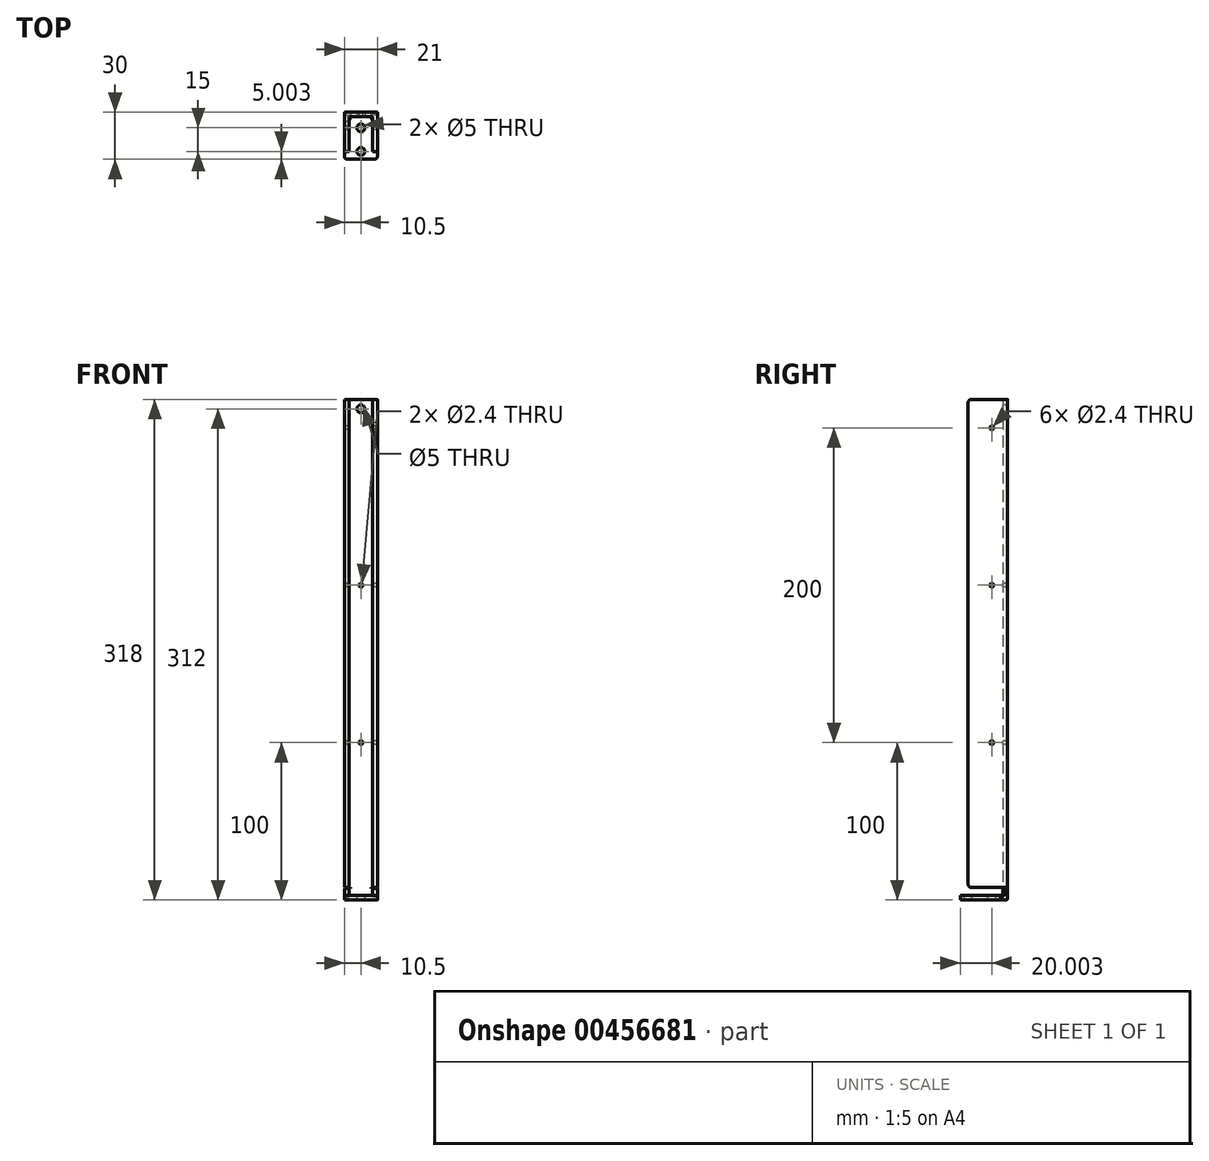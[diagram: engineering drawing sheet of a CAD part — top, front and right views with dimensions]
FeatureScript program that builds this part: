
annotation { "Feature Type Name" : "Feature", "Feature Type Description" : "" }
export const myFeature = defineFeature(function(context is Context, id is Id, definition is map)
    precondition{}
    {
        {
            var Q0;
            Q0=qCreatedBy(makeId("Right.planeOp"),FACE);
            var sketch = newSketch(context, id + "F0", { "sketchPlane" : qUnion([Q0])});
            skLineSegment(sketch, "E0", {"start": v(-7.6, 0) * mm, "end": v(22.4, 0) * mm});
            skLineSegment(sketch, "E1", {"start": v(22.4, 0) * mm, "end": v(22.4, 318) * mm});
            skLineSegment(sketch, "E2", {"start": v(22.4, 318) * mm, "end": v(19.4, 318) * mm});
            skLineSegment(sketch, "E3", {"start": v(19.4, 318) * mm, "end": v(19.4, 3) * mm});
            skLineSegment(sketch, "E4", {"start": v(19.4, 3) * mm, "end": v(-7.6, 3) * mm});
            skLineSegment(sketch, "E5", {"start": v(-7.6, 3) * mm, "end": v(-7.6, 0) * mm});
            skSolve(sketch);
        }
        {
            var Q0;
            Q0=qSketchRegion(id+"F0",true);
            extrude(context, id + "F1", {"entities" : qUnion([Q0]), "depth" : 15 * mm});
        }
        {
            var Q0;
            Q0=makeQuery(id+"F1.opExtrude","SWEPT_FACE",FACE,{"disambiguationData":[OSD([sQuery(id+"F0.wireOp",EDGE,"E1")])]});
            var sketch = newSketch(context, id + "F2", { "sketchPlane" : qUnion([Q0])});
            skLineSegment(sketch, "E6.bottom", {"start": v(0, 8) * mm, "end": v(3, 8) * mm});
            skLineSegment(sketch, "E6.top", {"start": v(0, 318) * mm, "end": v(3, 318) * mm});
            skLineSegment(sketch, "E6.left", {"start": v(0, 8) * mm, "end": v(0, 318) * mm});
            skLineSegment(sketch, "E6.right", {"start": v(3, 8) * mm, "end": v(3, 318) * mm});
            skLineSegment(sketch, "E7.bottom", {"start": v(-15, 318) * mm, "end": v(-18, 318) * mm});
            skLineSegment(sketch, "E7.top", {"start": v(-15, 8) * mm, "end": v(-18, 8) * mm});
            skLineSegment(sketch, "E7.left", {"start": v(-15, 318) * mm, "end": v(-15, 8) * mm});
            skLineSegment(sketch, "E7.right", {"start": v(-18, 318) * mm, "end": v(-18, 8) * mm});
            skSolve(sketch);
        }
        {
            var Q0;
            Q0=qSketchRegion(id+"F2",true);
            extrude(context, id + "F3", {"entities" : qUnion([Q0]), "operationType" : NewBodyOperationType.ADD, "oppositeDirection" : true, "depth" : 25 * mm});
        }
        {
            var Q0;
            Q0=makeQuery(id+"F1.opExtrude","SWEPT_FACE",FACE,{"disambiguationData":[OSD([sQuery(id+"F0.wireOp",EDGE,"E4")])]});
            var sketch = newSketch(context, id + "F4", { "sketchPlane" : qUnion([Q0])});
            skCircle(sketch, "E8", {"center": v(7.5, -2.6) * mm, "radius": 2.5 * mm});
            skCircle(sketch, "E9", {"center": v(7.5, 12.4) * mm, "radius": 2.5 * mm});
            skCircle(sketch, "E10", {"center": v(7.5, 12.4) * mm, "radius": 4.5 * mm, "construction": true});
            skCircle(sketch, "E11", {"center": v(7.5, -2.6) * mm, "radius": 4.46 * mm, "construction": true});
            skSolve(sketch);
        }
        {
            var Q0;
            Q0=qSketchRegion(id+"F4",true);
            extrude(context, id + "F5", {"entities" : qUnion([Q0]), "operationType" : NewBodyOperationType.REMOVE, "oppositeDirection" : true, "depth" : 3 * mm});
        }
        {
            var Q0;
            Q0=makeQuery(id+"F1.opExtrude","SWEPT_FACE",FACE,{"disambiguationData":[OSD([sQuery(id+"F0.wireOp",EDGE,"E3")])]});
            var sketch = newSketch(context, id + "F6", { "sketchPlane" : qUnion([Q0])});
            skLineSegment(sketch, "E12.bottom", {"start": v(0, 8) * mm, "end": v(1, 8) * mm});
            skLineSegment(sketch, "E12.top", {"start": v(0, 7.5) * mm, "end": v(1, 7.5) * mm});
            skLineSegment(sketch, "E12.left", {"start": v(0, 8) * mm, "end": v(0, 7.5) * mm});
            skLineSegment(sketch, "E12.right", {"start": v(1, 8) * mm, "end": v(1, 7.5) * mm});
            skLineSegment(sketch, "E13.bottom", {"start": v(15, 8) * mm, "end": v(14, 8) * mm});
            skLineSegment(sketch, "E13.top", {"start": v(15, 7.5) * mm, "end": v(14, 7.5) * mm});
            skLineSegment(sketch, "E13.left", {"start": v(15, 8) * mm, "end": v(15, 7.5) * mm});
            skLineSegment(sketch, "E13.right", {"start": v(14, 8) * mm, "end": v(14, 7.5) * mm});
            skSolve(sketch);
        }
        {
            var Q0;
            Q0=qSketchRegion(id+"F6",true);
            extrude(context, id + "F7", {"entities" : qUnion([Q0]), "operationType" : NewBodyOperationType.REMOVE, "oppositeDirection" : true, "depth" : 3 * mm});
        }
        {
            var Q0;
            Q0=makeQuery(id+"F1.opExtrude","SWEPT_EDGE",EDGE,{"disambiguationData":[OSD([sQuery(id+"F0.wireOp",EDGE,"E3"),sQuery(id+"F0.wireOp",EDGE,"E4")])]});
            var Q1;
            Q1=makeQuery(id+"F1.opExtrude","SWEPT_EDGE",EDGE,{"disambiguationData":[OSD([sQuery(id+"F0.wireOp",EDGE,"E0"),sQuery(id+"F0.wireOp",EDGE,"E1")])]});
            var Q2;
            {var subQ0=sQuery(id+"F0.wireOp",EDGE,"E3");Q2=makeQuery(id+"F3.boolean.opBoolean","SPLIT",EDGE,{"disambiguationData":[topologyDisambiguationEdgeConnected([makeQuery(id+"F3.opExtrude","SWEPT_FACE",FACE,{"disambiguationData":[OSD([sQuery(id+"F2.wireOp",EDGE,"E6.left")])]})])],"derivedFrom":makeQuery(id+"F1.opExtrude","CAP_EDGE",EDGE,{"disambiguationData":[OSD([subQ0])],"isStart":true})});}
            var Q3;
            Q3=makeQuery(id+"F3.opExtrude","CAP_EDGE",EDGE,{"disambiguationData":[OSD([sQuery(id+"F2.wireOp",EDGE,"E6.right")])],"isStart":true});
            var Q4;
            Q4=makeQuery(id+"F3.opExtrude","CAP_EDGE",EDGE,{"disambiguationData":[OSD([sQuery(id+"F2.wireOp",EDGE,"E7.right")])],"isStart":true});
            var Q5;
            {var subQ0=sQuery(id+"F0.wireOp",EDGE,"E3");Q5=makeQuery(id+"F3.boolean.opBoolean","SPLIT",EDGE,{"disambiguationData":[topologyDisambiguationEdgeConnected([makeQuery(id+"F3.opExtrude","SWEPT_FACE",FACE,{"disambiguationData":[OSD([sQuery(id+"F2.wireOp",EDGE,"E7.left")])]})])],"derivedFrom":makeQuery(id+"F1.opExtrude","CAP_EDGE",EDGE,{"disambiguationData":[OSD([subQ0])],"isStart":false})});}
            var Q6;
            Q6=makeQuery(id+"FqQp6dOOzKqRe4i_1.boolean.opBoolean","COPY",EDGE,{"derivedFrom":makeQuery(id+"FqQp6dOOzKqRe4i_1.opExtrude","CAP_EDGE",EDGE,{"disambiguationData":[OSD([sQuery(id+"FuQxhJIuyBZaYl9_1.wireOp",EDGE,"ZrIXolOl-gWOG-G3Ii-Wei4-7PRN7w7ykNvu.left")])],"isStart":false})});
            var Q7;
            Q7=makeQuery(id+"FqQp6dOOzKqRe4i_1.boolean.opBoolean","COPY",EDGE,{"derivedFrom":makeQuery(id+"FqQp6dOOzKqRe4i_1.opExtrude","CAP_EDGE",EDGE,{"disambiguationData":[OSD([sQuery(id+"FuQxhJIuyBZaYl9_1.wireOp",EDGE,"ZrIXolOl-gWOG-G3Ii-Wei4-7PRN7w7ykNvu.right")])],"isStart":false})});
            fillet(context, id + "F8", {"entities" : qUnion([Q0, Q1, Q2, Q3, Q4, Q5, Q6, Q7]), "radius" : 1 * mm, "tangentPropagation" : true, "allowEdgeOverflow" : false});
        }
        {
            var Q0;
            Q0=makeQuery(id+"F1.opExtrude","SWEPT_FACE",FACE,{"disambiguationData":[OSD([sQuery(id+"F0.wireOp",EDGE,"E3")])]});
            var sketch = newSketch(context, id + "F9", { "sketchPlane" : qUnion([Q0])});
            skCircle(sketch, "E14", {"center": v(7.5, 312) * mm, "radius": 2.5 * mm});
            skPoint(sketch, "E14.centerSnap0", {"position": v(7.5, 318) * mm});
            skCircle(sketch, "E15", {"center": v(7.5, 100) * mm, "radius": 1.2 * mm});
            skPoint(sketch, "E15.centerSnap0", {"position": v(7.5, 4) * mm});
            skCircle(sketch, "E16", {"center": v(7.5, 200) * mm, "radius": 1.2 * mm});
            skSolve(sketch);
        }
        {
            var Q0;
            Q0=qSketchRegion(id+"F9",true);
            extrude(context, id + "F10", {"entities" : qUnion([Q0]), "operationType" : NewBodyOperationType.REMOVE, "oppositeDirection" : true, "depth" : 3 * mm});
        }
        {
            var Q0;
            Q0=makeQuery(id+"F3.opExtrude","SWEPT_FACE",FACE,{"disambiguationData":[OSD([sQuery(id+"F2.wireOp",EDGE,"E6.right")])]});
            var sketch = newSketch(context, id + "F11", { "sketchPlane" : qUnion([Q0])});
            skCircle(sketch, "E17", {"center": v(-12.4, 300) * mm, "radius": 1.2 * mm});
            skCircle(sketch, "E18", {"center": v(-12.4, 100) * mm, "radius": 1.2 * mm});
            skLineSegment(sketch, "E19", {"start": v(-14.4, 98) * mm, "end": v(-14.4, -49.26) * mm, "construction": true});
            skLineSegment(sketch, "E20", {"start": v(103.6, 103.79) * mm, "end": v(103.6, -31.5) * mm, "construction": true});
            skLineSegment(sketch, "E21", {"start": v(-16.4, 98.96) * mm, "end": v(-16.4, 90.53) * mm, "construction": true});
            skLineSegment(sketch, "E22", {"start": v(105.6, 89.13) * mm, "end": v(105.6, 82.47) * mm, "construction": true});
            skCircle(sketch, "E23", {"center": v(-12.4, 200) * mm, "radius": 1.2 * mm});
            skSolve(sketch);
        }
        {
            var Q0;
            Q0=qSketchRegion(id+"F11",true);
            extrude(context, id + "F12", {"entities" : qUnion([Q0]), "operationType" : NewBodyOperationType.REMOVE, "oppositeDirection" : true, "depth" : 34.2 * mm});
        }
        {
            var Q0;
            Q0=makeQuery(id+"F1.opExtrude","CAP_FACE",FACE,{"disambiguationData":[OSD([sQuery(id+"F0.wireOp",EDGE,"E0"),sQuery(id+"F0.wireOp",EDGE,"E1"),sQuery(id+"F0.wireOp",EDGE,"E2"),sQuery(id+"F0.wireOp",EDGE,"E3"),sQuery(id+"F0.wireOp",EDGE,"E4"),sQuery(id+"F0.wireOp",EDGE,"E5")])],"isStart":true});
            extrude(context, id + "F13", {"entities" : qUnion([Q0]), "operationType" : NewBodyOperationType.ADD, "depth" : 3 * mm});
        }
        {
            var Q0;
            Q0=makeQuery(id+"F1.opExtrude","CAP_FACE",FACE,{"disambiguationData":[OSD([sQuery(id+"F0.wireOp",EDGE,"E0"),sQuery(id+"F0.wireOp",EDGE,"E1"),sQuery(id+"F0.wireOp",EDGE,"E2"),sQuery(id+"F0.wireOp",EDGE,"E3"),sQuery(id+"F0.wireOp",EDGE,"E4"),sQuery(id+"F0.wireOp",EDGE,"E5")])],"isStart":false});
            extrude(context, id + "F14", {"entities" : qUnion([Q0]), "operationType" : NewBodyOperationType.ADD, "depth" : 3 * mm});
        }
        {
            var Q0;
            Q0=makeQuery(id+"F3.opExtrude","CAP_EDGE",EDGE,{"disambiguationData":[OSD([sQuery(id+"F2.wireOp",EDGE,"E6.bottom")])],"isStart":false});
            var Q1;
            Q1=makeQuery(id+"F3.opExtrude","CAP_EDGE",EDGE,{"disambiguationData":[OSD([sQuery(id+"F2.wireOp",EDGE,"E7.top")])],"isStart":false});
            var Q2;
            Q2=makeQuery(id+"F13.opExtrude","CAP_EDGE",EDGE,{"disambiguationData":[OSD([sQuery(id+"F0.wireOp",EDGE,"E5")])],"isStart":false});
            var Q3;
            Q3=makeQuery(id+"F14.opExtrude","CAP_EDGE",EDGE,{"disambiguationData":[OSD([sQuery(id+"F0.wireOp",EDGE,"E5")])],"isStart":false});
            var Q4;
            Q4=makeQuery(id+"F3.opExtrude","CAP_EDGE",EDGE,{"disambiguationData":[OSD([sQuery(id+"F2.wireOp",EDGE,"E6.top")])],"isStart":false});
            var Q5;
            Q5=makeQuery(id+"F3.opExtrude","CAP_EDGE",EDGE,{"disambiguationData":[OSD([sQuery(id+"F2.wireOp",EDGE,"E7.bottom")])],"isStart":false});
            fillet(context, id + "F15", {"entities" : qUnion([Q0, Q1, Q2, Q3, Q4, Q5]), "radius" : 2 * mm, "tangentPropagation" : true, "allowEdgeOverflow" : false});
        }
    });
